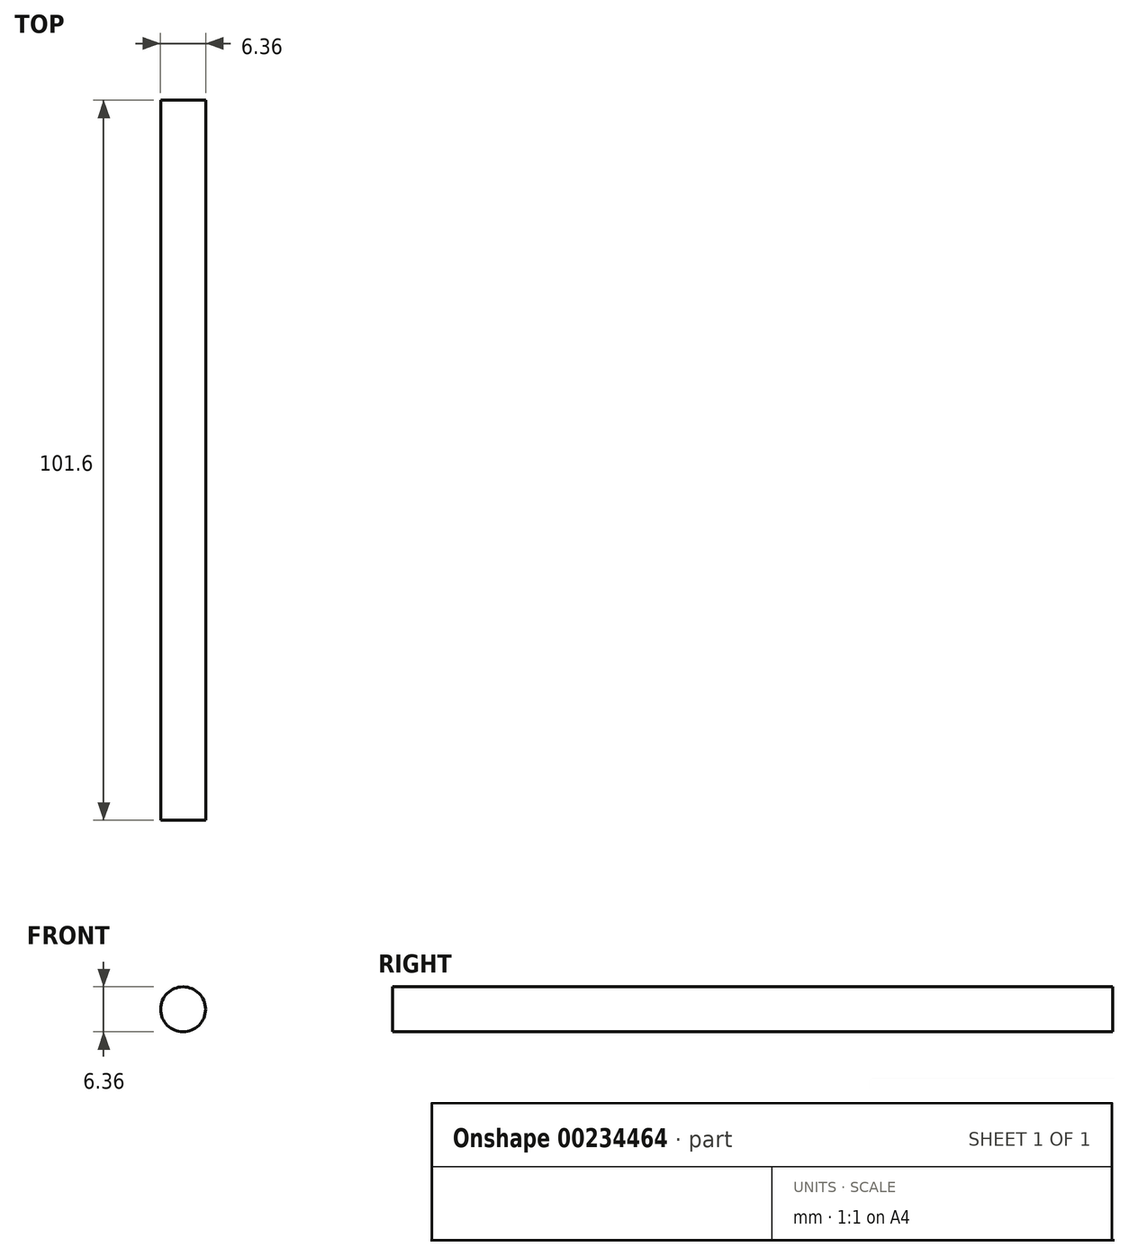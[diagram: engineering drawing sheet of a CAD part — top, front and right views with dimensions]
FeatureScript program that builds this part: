
annotation { "Feature Type Name" : "Feature", "Feature Type Description" : "" }
export const myFeature = defineFeature(function(context is Context, id is Id, definition is map)
    precondition{}
    {
        {
            var Q0;
            Q0=qCreatedBy(makeId("Front.planeOp"),FACE);
            var sketch = newSketch(context, id + "F0", { "sketchPlane" : qUnion([Q0])});
            skCircle(sketch, "E0", {"center": v(0, 0) * mm, "radius": 3.18 * mm});
            skSolve(sketch);
        }
        {
            var Q0;
            Q0 = qSketchRegion(id + "F0", true);
            extrude(context, id + "F1", {"entities" : qUnion([Q0]), "depth" : 101.6 * mm});
        }
    });
